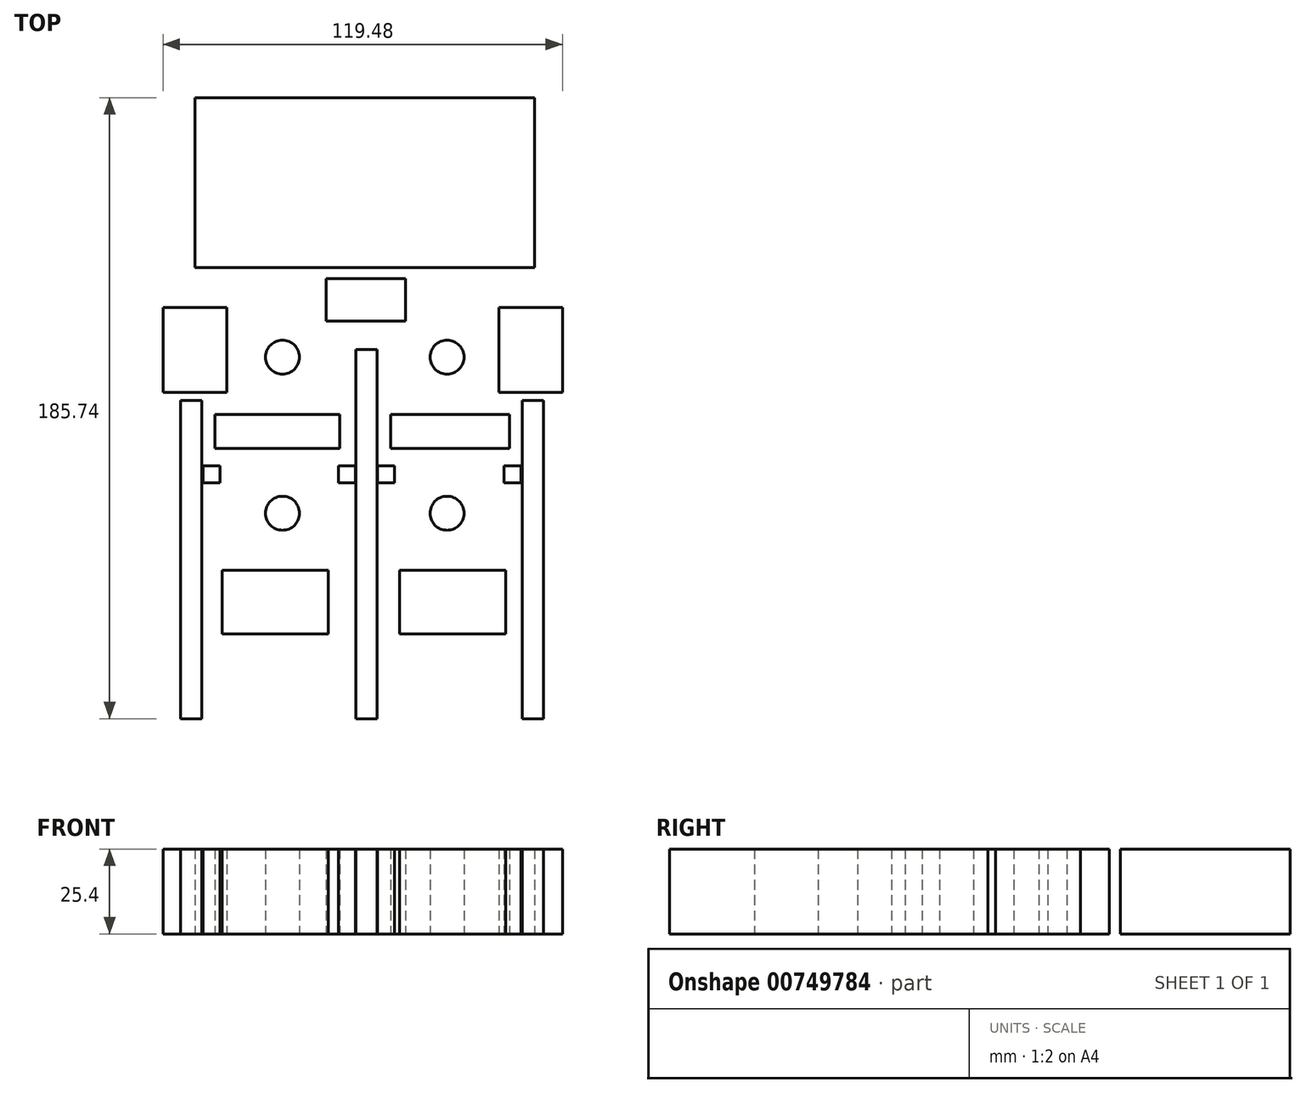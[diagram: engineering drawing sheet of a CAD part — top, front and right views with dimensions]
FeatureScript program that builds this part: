
annotation { "Feature Type Name" : "Feature", "Feature Type Description" : "" }
export const myFeature = defineFeature(function(context is Context, id is Id, definition is map)
    precondition{}
    {
        {
            var Q0;
            Q0=qCreatedBy(makeId("Top.planeOp"),FACE);
            var sketch = newSketch(context, id + "F0", { "sketchPlane" : qUnion([Q0])});
            skLineSegment(sketch, "E0.bottom", {"start": v(0, 0) * mm, "end": v(101.6, 0) * mm});
            skLineSegment(sketch, "E0.top", {"start": v(0, 50.8) * mm, "end": v(101.6, 50.8) * mm});
            skLineSegment(sketch, "E0.left", {"start": v(0, 0) * mm, "end": v(0, 50.8) * mm});
            skLineSegment(sketch, "E0.right", {"start": v(101.6, 0) * mm, "end": v(101.6, 50.8) * mm});
            skSolve(sketch);
        }
        {
            var Q0;
            Q0 = qSketchRegion(id + "F0", true);
            extrude(context, id + "F1", {"entities" : qUnion([Q0]), "depth" : 25.4 * mm, "offsetDistance" : 25.4 * mm});
        }
        {
            var Q0;
            Q0=qCreatedBy(makeId("Top.planeOp"),FACE);
            var sketch = newSketch(context, id + "F2", { "sketchPlane" : qUnion([Q0])});
            skLineSegment(sketch, "E1.bottom", {"start": v(-9.53, -11.9) * mm, "end": v(9.53, -11.9) * mm});
            skLineSegment(sketch, "E1.top", {"start": v(-9.53, -37.3) * mm, "end": v(9.53, -37.3) * mm});
            skLineSegment(sketch, "E1.left", {"start": v(-9.53, -11.9) * mm, "end": v(-9.53, -37.3) * mm});
            skLineSegment(sketch, "E1.right", {"start": v(9.53, -11.9) * mm, "end": v(9.53, -37.3) * mm});
            skPoint(sketch, "E1.middle", {"position": v(0, -24.6) * mm});
            skLineSegment(sketch, "E2.bottom", {"start": v(90.9, -11.9) * mm, "end": v(109.95, -11.9) * mm});
            skLineSegment(sketch, "E2.top", {"start": v(90.9, -37.3) * mm, "end": v(109.95, -37.3) * mm});
            skLineSegment(sketch, "E2.left", {"start": v(90.9, -11.9) * mm, "end": v(90.9, -37.3) * mm});
            skLineSegment(sketch, "E2.right", {"start": v(109.95, -11.9) * mm, "end": v(109.95, -37.3) * mm});
            skPoint(sketch, "E2.middle", {"position": v(100.42, -24.6) * mm});
            skSolve(sketch);
        }
        {
            var Q0;
            Q0 = qSketchRegion(id + "F2", true);
            extrude(context, id + "F3", {"entities" : qUnion([Q0]), "depth" : 25.4 * mm, "offsetDistance" : 25.4 * mm});
        }
        {
            var Q0;
            Q0=qCreatedBy(makeId("Top.planeOp"),FACE);
            var sketch = newSketch(context, id + "F4", { "sketchPlane" : qUnion([Q0])});
            skLineSegment(sketch, "E3.bottom", {"start": v(39.23, -3.31) * mm, "end": v(63.06, -3.31) * mm});
            skLineSegment(sketch, "E3.top", {"start": v(39.23, -16.04) * mm, "end": v(63.06, -16.04) * mm});
            skLineSegment(sketch, "E3.left", {"start": v(39.23, -3.31) * mm, "end": v(39.23, -16.04) * mm});
            skLineSegment(sketch, "E3.right", {"start": v(63.06, -3.31) * mm, "end": v(63.06, -16.04) * mm});
            skLineSegment(sketch, "E4.bottom", {"start": v(48.14, -24.45) * mm, "end": v(54.5, -24.45) * mm});
            skLineSegment(sketch, "E4.top", {"start": v(48.14, -109.54) * mm, "end": v(54.5, -109.54) * mm});
            skLineSegment(sketch, "E4.left", {"start": v(48.14, -24.45) * mm, "end": v(48.14, -109.54) * mm});
            skLineSegment(sketch, "E4.right", {"start": v(54.5, -24.45) * mm, "end": v(54.5, -109.54) * mm});
            skLineSegment(sketch, "E5.bottom", {"start": v(97.98, -39.7) * mm, "end": v(104.33, -39.7) * mm});
            skLineSegment(sketch, "E5.top", {"start": v(97.98, -109.54) * mm, "end": v(104.33, -109.54) * mm});
            skLineSegment(sketch, "E5.left", {"start": v(97.98, -39.7) * mm, "end": v(97.98, -109.54) * mm});
            skLineSegment(sketch, "E5.right", {"start": v(104.33, -39.7) * mm, "end": v(104.33, -109.54) * mm});
            skLineSegment(sketch, "E6.bottom", {"start": v(2.1, -39.7) * mm, "end": v(-4.24, -39.7) * mm});
            skLineSegment(sketch, "E6.top", {"start": v(2.1, -109.54) * mm, "end": v(-4.24, -109.54) * mm});
            skLineSegment(sketch, "E6.left", {"start": v(2.1, -39.7) * mm, "end": v(2.1, -109.54) * mm});
            skLineSegment(sketch, "E6.right", {"start": v(-4.24, -39.7) * mm, "end": v(-4.24, -109.54) * mm});
            skLineSegment(sketch, "E7.bottom", {"start": v(6.02, -43.98) * mm, "end": v(43.36, -43.98) * mm});
            skLineSegment(sketch, "E7.top", {"start": v(6.02, -54.14) * mm, "end": v(43.36, -54.14) * mm});
            skLineSegment(sketch, "E7.left", {"start": v(6.02, -43.98) * mm, "end": v(6.02, -54.14) * mm});
            skLineSegment(sketch, "E7.right", {"start": v(43.36, -43.98) * mm, "end": v(43.36, -54.14) * mm});
            skLineSegment(sketch, "E8.bottom", {"start": v(58.53, -43.98) * mm, "end": v(94.1, -43.98) * mm});
            skLineSegment(sketch, "E8.top", {"start": v(58.53, -54.14) * mm, "end": v(94.1, -54.14) * mm});
            skLineSegment(sketch, "E8.left", {"start": v(58.53, -43.98) * mm, "end": v(58.53, -54.14) * mm});
            skLineSegment(sketch, "E8.right", {"start": v(94.1, -43.98) * mm, "end": v(94.1, -54.14) * mm});
            skLineSegment(sketch, "E9.bottom", {"start": v(8.12, -109.54) * mm, "end": v(39.87, -109.54) * mm});
            skLineSegment(sketch, "E9.top", {"start": v(8.12, -90.5) * mm, "end": v(39.87, -90.5) * mm});
            skLineSegment(sketch, "E9.left", {"start": v(8.12, -109.54) * mm, "end": v(8.12, -90.5) * mm});
            skLineSegment(sketch, "E9.right", {"start": v(39.87, -109.54) * mm, "end": v(39.87, -90.5) * mm});
            skLineSegment(sketch, "E10.bottom", {"start": v(61.26, -109.54) * mm, "end": v(93.01, -109.54) * mm});
            skLineSegment(sketch, "E10.top", {"start": v(61.26, -90.5) * mm, "end": v(93.01, -90.5) * mm});
            skLineSegment(sketch, "E10.left", {"start": v(61.26, -109.54) * mm, "end": v(61.26, -90.5) * mm});
            skLineSegment(sketch, "E10.right", {"start": v(93.01, -109.54) * mm, "end": v(93.01, -90.5) * mm});
            skSolve(sketch);
        }
        {
            var Q0;
            Q0 = qSketchRegion(id + "F4", true);
            extrude(context, id + "F5", {"entities" : qUnion([Q0]), "depth" : 25.4 * mm, "offsetDistance" : 25.4 * mm});
        }
        {
            var Q0;
            Q0=qCreatedBy(makeId("Top.planeOp"),FACE);
            var sketch = newSketch(context, id + "F6", { "sketchPlane" : qUnion([Q0])});
            skLineSegment(sketch, "E11.bottom", {"start": v(2.4, -59.35) * mm, "end": v(7.47, -59.35) * mm});
            skLineSegment(sketch, "E11.top", {"start": v(2.4, -64.43) * mm, "end": v(7.47, -64.43) * mm});
            skLineSegment(sketch, "E11.left", {"start": v(2.4, -59.35) * mm, "end": v(2.4, -64.43) * mm});
            skLineSegment(sketch, "E11.right", {"start": v(7.47, -59.35) * mm, "end": v(7.47, -64.43) * mm});
            skLineSegment(sketch, "E12.bottom", {"start": v(48.05, -64.43) * mm, "end": v(42.97, -64.43) * mm});
            skLineSegment(sketch, "E12.top", {"start": v(48.05, -59.35) * mm, "end": v(42.97, -59.35) * mm});
            skLineSegment(sketch, "E12.left", {"start": v(48.05, -64.43) * mm, "end": v(48.05, -59.35) * mm});
            skLineSegment(sketch, "E12.right", {"start": v(42.97, -64.43) * mm, "end": v(42.97, -59.35) * mm});
            skLineSegment(sketch, "E13.bottom", {"start": v(54.66, -64.43) * mm, "end": v(59.74, -64.43) * mm});
            skLineSegment(sketch, "E13.top", {"start": v(54.66, -59.35) * mm, "end": v(59.74, -59.35) * mm});
            skLineSegment(sketch, "E13.left", {"start": v(54.66, -64.43) * mm, "end": v(54.66, -59.35) * mm});
            skLineSegment(sketch, "E13.right", {"start": v(59.74, -64.43) * mm, "end": v(59.74, -59.35) * mm});
            skLineSegment(sketch, "E14.bottom", {"start": v(97.58, -64.43) * mm, "end": v(92.5, -64.43) * mm});
            skLineSegment(sketch, "E14.top", {"start": v(97.58, -59.35) * mm, "end": v(92.5, -59.35) * mm});
            skLineSegment(sketch, "E14.left", {"start": v(97.58, -64.43) * mm, "end": v(97.58, -59.35) * mm});
            skLineSegment(sketch, "E14.right", {"start": v(92.5, -64.43) * mm, "end": v(92.5, -59.35) * mm});
            skLineSegment(sketch, "E15", {"start": v(0, 0) * mm, "end": v(0, -59.35) * mm, "construction": true});
            skLineSegment(sketch, "E16", {"start": v(0, -59.35) * mm, "end": v(2.4, -59.35) * mm, "construction": true});
            skLineSegment(sketch, "E17", {"start": v(7.47, -64.43) * mm, "end": v(42.97, -64.43) * mm, "construction": true});
            skLineSegment(sketch, "E18", {"start": v(48.05, -64.43) * mm, "end": v(54.66, -64.43) * mm, "construction": true});
            skLineSegment(sketch, "E19", {"start": v(59.74, -64.43) * mm, "end": v(92.5, -64.43) * mm, "construction": true});
            skSolve(sketch);
        }
        {
            var Q0;
            Q0=makeQuery(id+"F6.imprint","IMPRINT",FACE,{"disambiguationData":[TD([[makeQuery(id+"F6.imprint","IMPRINT",EDGE,{"derivedFrom":sQuery(id+"F6.wireOp",EDGE,"E11.bottom")}),-1.0]])]});
            var Q1;
            Q1=makeQuery(id+"F6.imprint","IMPRINT",FACE,{"disambiguationData":[TD([[makeQuery(id+"F6.imprint","IMPRINT",EDGE,{"derivedFrom":sQuery(id+"F6.wireOp",EDGE,"E12.bottom")}),-1.0]])]});
            var Q2;
            Q2=makeQuery(id+"F6.imprint","IMPRINT",FACE,{"disambiguationData":[TD([[makeQuery(id+"F6.imprint","IMPRINT",EDGE,{"derivedFrom":sQuery(id+"F6.wireOp",EDGE,"E13.bottom")}),1.0]])]});
            var Q3;
            Q3=makeQuery(id+"F6.imprint","IMPRINT",FACE,{"disambiguationData":[TD([[makeQuery(id+"F6.imprint","IMPRINT",EDGE,{"derivedFrom":sQuery(id+"F6.wireOp",EDGE,"E14.bottom")}),-1.0]])]});
            extrude(context, id + "F7", {"entities" : qUnion([Q0, Q1, Q2, Q3]), "depth" : 25.4 * mm, "offsetDistance" : 25.4 * mm});
        }
        {
            var Q0;
            Q0=qCreatedBy(makeId("Top.planeOp"),FACE);
            var sketch = newSketch(context, id + "F8", { "sketchPlane" : qUnion([Q0])});
            skCircle(sketch, "E20", {"center": v(26.21, -26.78) * mm, "radius": 5.08 * mm});
            skCircle(sketch, "E21", {"center": v(75.42, -26.78) * mm, "radius": 5.08 * mm});
            skCircle(sketch, "E22", {"center": v(26.21, -73.5) * mm, "radius": 5.08 * mm});
            skCircle(sketch, "E23", {"center": v(75.42, -73.5) * mm, "radius": 5.08 * mm});
            skSolve(sketch);
        }
        {
            var Q0;
            Q0=makeQuery(id+"F8.imprint","IMPRINT",FACE,{"disambiguationData":[TD([[makeQuery(id+"F8.imprint","IMPRINT",EDGE,{"derivedFrom":sQuery(id+"F8.wireOp",EDGE,"E20")}),1.0]])]});
            var Q1;
            Q1=makeQuery(id+"F8.imprint","IMPRINT",FACE,{"disambiguationData":[TD([[makeQuery(id+"F8.imprint","IMPRINT",EDGE,{"derivedFrom":sQuery(id+"F8.wireOp",EDGE,"E21")}),1.0]])]});
            var Q2;
            Q2=makeQuery(id+"F8.imprint","IMPRINT",FACE,{"disambiguationData":[TD([[makeQuery(id+"F8.imprint","IMPRINT",EDGE,{"derivedFrom":sQuery(id+"F8.wireOp",EDGE,"E23")}),1.0]])]});
            var Q3;
            Q3=makeQuery(id+"F8.imprint","IMPRINT",FACE,{"disambiguationData":[TD([[makeQuery(id+"F8.imprint","IMPRINT",EDGE,{"derivedFrom":sQuery(id+"F8.wireOp",EDGE,"E22")}),1.0]])]});
            extrude(context, id + "F9", {"entities" : qUnion([Q0, Q1, Q2, Q3]), "depth" : 25.4 * mm, "offsetDistance" : 25.4 * mm});
        }
        {
            var Q0;
            Q0=makeQuery(id+"F5.opExtrude","SWEPT_FACE",FACE,{"disambiguationData":[OSD([sQuery(id+"F4.wireOp",EDGE,"E4.top")])]});
            var sketch = newSketch(context, id + "F10", { "sketchPlane" : qUnion([Q0])});
            skLineSegment(sketch, "E24.bottom", {"start": v(48.14, 25.4) * mm, "end": v(54.5, 25.4) * mm});
            skLineSegment(sketch, "E24.top", {"start": v(48.14, 0) * mm, "end": v(54.5, 0) * mm});
            skLineSegment(sketch, "E24.left", {"start": v(48.14, 25.4) * mm, "end": v(48.14, 0) * mm});
            skLineSegment(sketch, "E24.right", {"start": v(54.5, 25.4) * mm, "end": v(54.5, 0) * mm});
            skSolve(sketch);
        }
        {
            var Q0;
            Q0=makeQuery(id+"F10.imprint","IMPRINT",FACE,{"disambiguationData":[TD([[makeQuery(id+"F10.imprint","IMPRINT",EDGE,{"derivedFrom":sQuery(id+"F10.wireOp",EDGE,"E24.bottom")}),-1.0]])]});
            extrude(context, id + "F11", {"entities" : qUnion([Q0]), "operationType" : NewBodyOperationType.ADD, "depth" : 25.4 * mm, "offsetDistance" : 25.4 * mm});
        }
        {
            var Q0;
            Q0=makeQuery(id+"F5.opExtrude","SWEPT_FACE",FACE,{"disambiguationData":[OSD([sQuery(id+"F4.wireOp",EDGE,"E5.top")])]});
            var sketch = newSketch(context, id + "F12", { "sketchPlane" : qUnion([Q0])});
            skLineSegment(sketch, "E25.bottom", {"start": v(97.98, 25.4) * mm, "end": v(104.33, 25.4) * mm});
            skLineSegment(sketch, "E25.top", {"start": v(97.98, 0) * mm, "end": v(104.33, 0) * mm});
            skLineSegment(sketch, "E25.left", {"start": v(97.98, 25.4) * mm, "end": v(97.98, 0) * mm});
            skLineSegment(sketch, "E25.right", {"start": v(104.33, 25.4) * mm, "end": v(104.33, 0) * mm});
            skSolve(sketch);
        }
        {
            var Q0;
            Q0 = qSketchRegion(id + "F12", true);
            extrude(context, id + "F13", {"entities" : qUnion([Q0]), "operationType" : NewBodyOperationType.ADD, "depth" : 25.4 * mm, "offsetDistance" : 25.4 * mm});
        }
        {
            var Q0;
            Q0=makeQuery(id+"F5.opExtrude","SWEPT_FACE",FACE,{"disambiguationData":[OSD([sQuery(id+"F4.wireOp",EDGE,"E6.top")])]});
            extrude(context, id + "F14", {"entities" : qUnion([Q0]), "operationType" : NewBodyOperationType.ADD, "depth" : 25.4 * mm, "offsetDistance" : 25.4 * mm});
        }
    });
